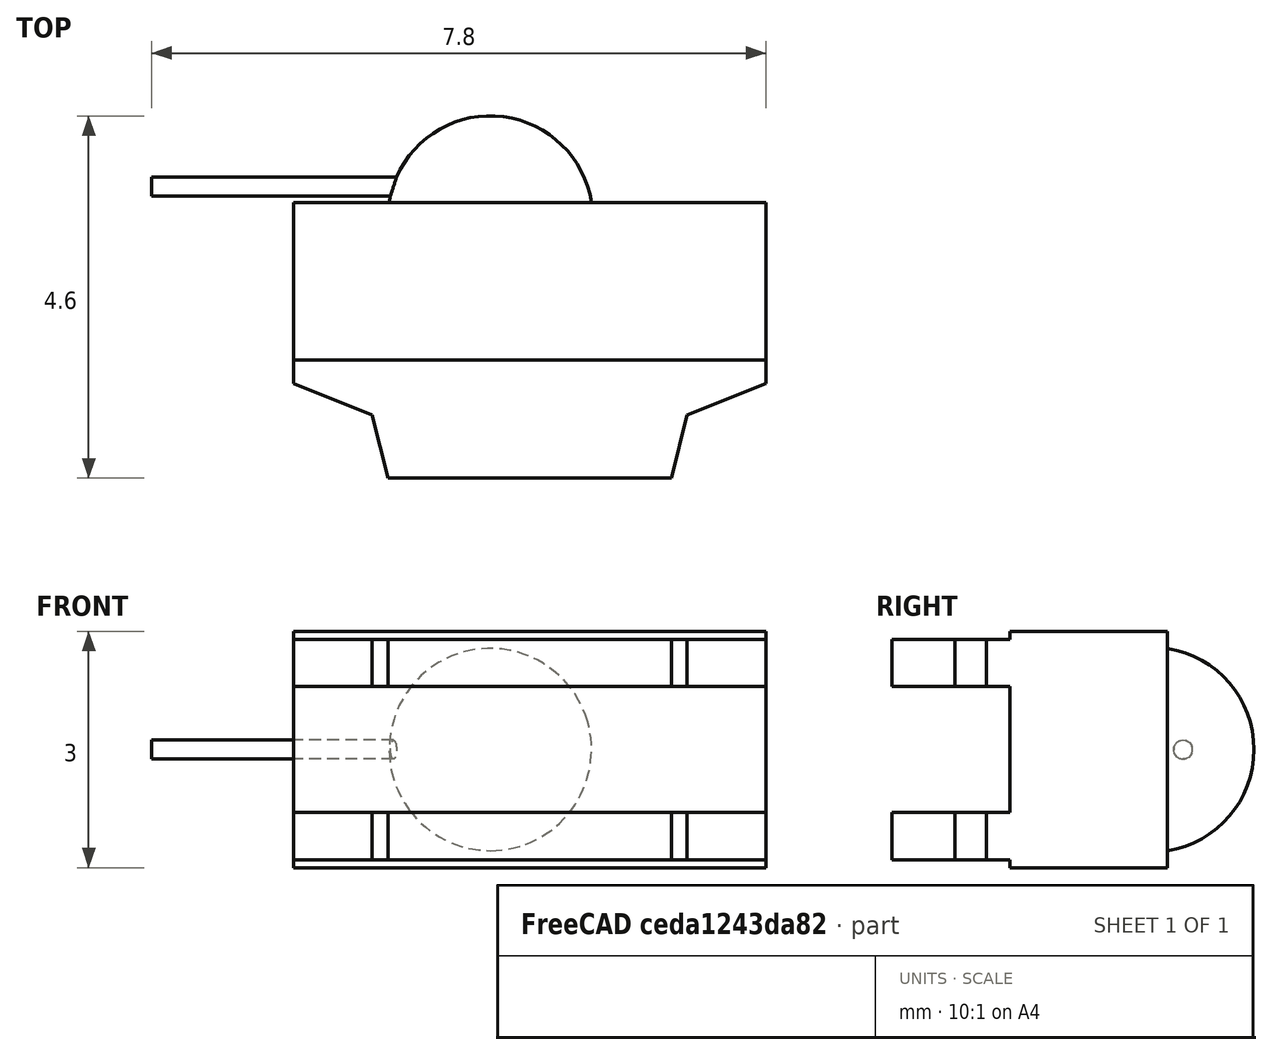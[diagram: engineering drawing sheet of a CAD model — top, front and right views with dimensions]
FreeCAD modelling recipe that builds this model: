
FCSTD DOCUMENT  (FreeCAD 0.15R4671 (Git))
Label: tank01
License: All rights reserved
LicenseURL: http://en.wikipedia.org/wiki/All_rights_reserved
objects: Mesh::Feature×5, Part::Fuse×4, Part::Part2DObjectPython×2, Part::Extrusion×2, Part::Feature×2, Part::Sphere×1, Part::Cylinder×1
note: 12 computed .brp shape members not serialized (recipe doc carries the construction recipe); baked Part::Feature solids carry a one-line shape summary decoded from their .brp

FEATURE [Part::Part2DObjectPython] DWire  # Draft 2D object (typed FeaturePython)
  ChamferSize = 0
  Closed = true
  End = (3,1.2,0)
  FilletRadius = 0
  Length = 14.0033
  MakeFace = true
  Points = (8) [(3,1.5,0),(-3,1.5,0),(-3,1.2,0),(-2,0.8,0),(-1.8,0,0),(1.8,0,0),(2,0.8,0),(3,1.2,0)]
  Start = (3,1.5,0)
FEATURE [Part::Extrusion] Extrude
  Base = -> DWire
  Dir = (0,0,0.6)
  Placement = pos=(0,-1.5,-1.4) rot=(0,0,1;0rad)
  Solid = true
FEATURE [Part::Part2DObjectPython] DWire001  # Draft 2D object (typed FeaturePython)
  ChamferSize = 0
  Closed = true
  End = (3,1.2,0)
  FilletRadius = 0
  Length = 14.0033
  MakeFace = true
  Points = (8) [(3,1.5,0),(-3,1.5,0),(-3,1.2,0),(-2,0.8,0),(-1.8,0,0),(1.8,0,0),(2,0.8,0),(3,1.2,0)]
  Start = (3,1.5,0)
FEATURE [Part::Extrusion] Extrude001
  Base = -> DWire001
  Dir = (0,0,0.6)
  Placement = pos=(0,-1.5,0.8) rot=(0,0,1;0rad)
  Solid = true
FEATURE [Mesh::Feature] body
  Placement = pos=(0,0,0) rot=(-1,0,0;1.5708rad)
FEATURE [Part::Sphere] Sphere
  Angle1 = -90
  Angle2 = 90
  Angle3 = 180
  Placement = pos=(-0.5,1.8,0) rot=(0,0,1;0rad)
  Radius = 1.3
FEATURE [Part::Cylinder] Cylinder
  Angle = 360
  Height = 4
  Placement = pos=(-0.8,2.2,0) rot=(0,-1,0;1.5708rad)
  Radius = 0.12
FEATURE [Mesh::Feature] Mesh  label="Extrude001 (Meshed)"
FEATURE [Mesh::Feature] Mesh001  label="Extrude (Meshed)"
FEATURE [Mesh::Feature] Mesh002  label="Sphere (Meshed)"
FEATURE [Mesh::Feature] Mesh003  label="Cylinder (Meshed)"
FEATURE [Part::Fuse] Fusion
  Base = -> Extrude
  Tool = -> Extrude001
FEATURE [Part::Fuse] Fusion001
  Base = -> Fusion
  Tool = -> Sphere
FEATURE [Part::Fuse] Fusion002
  Base = -> Fusion001
  Tool = -> Cylinder
FEATURE [Part::Feature] body001
  shape: bbox 6 x 2 x 3 mm, 12 faces, 0 solids (baked)
FEATURE [Part::Feature] body001_solid  label="body001 (Solid)"
  shape: bbox 6 x 2 x 3 mm, 12 faces (baked)
FEATURE [Part::Fuse] Fusion003
  Base = -> Fusion002
  Tool = -> body001_solid
